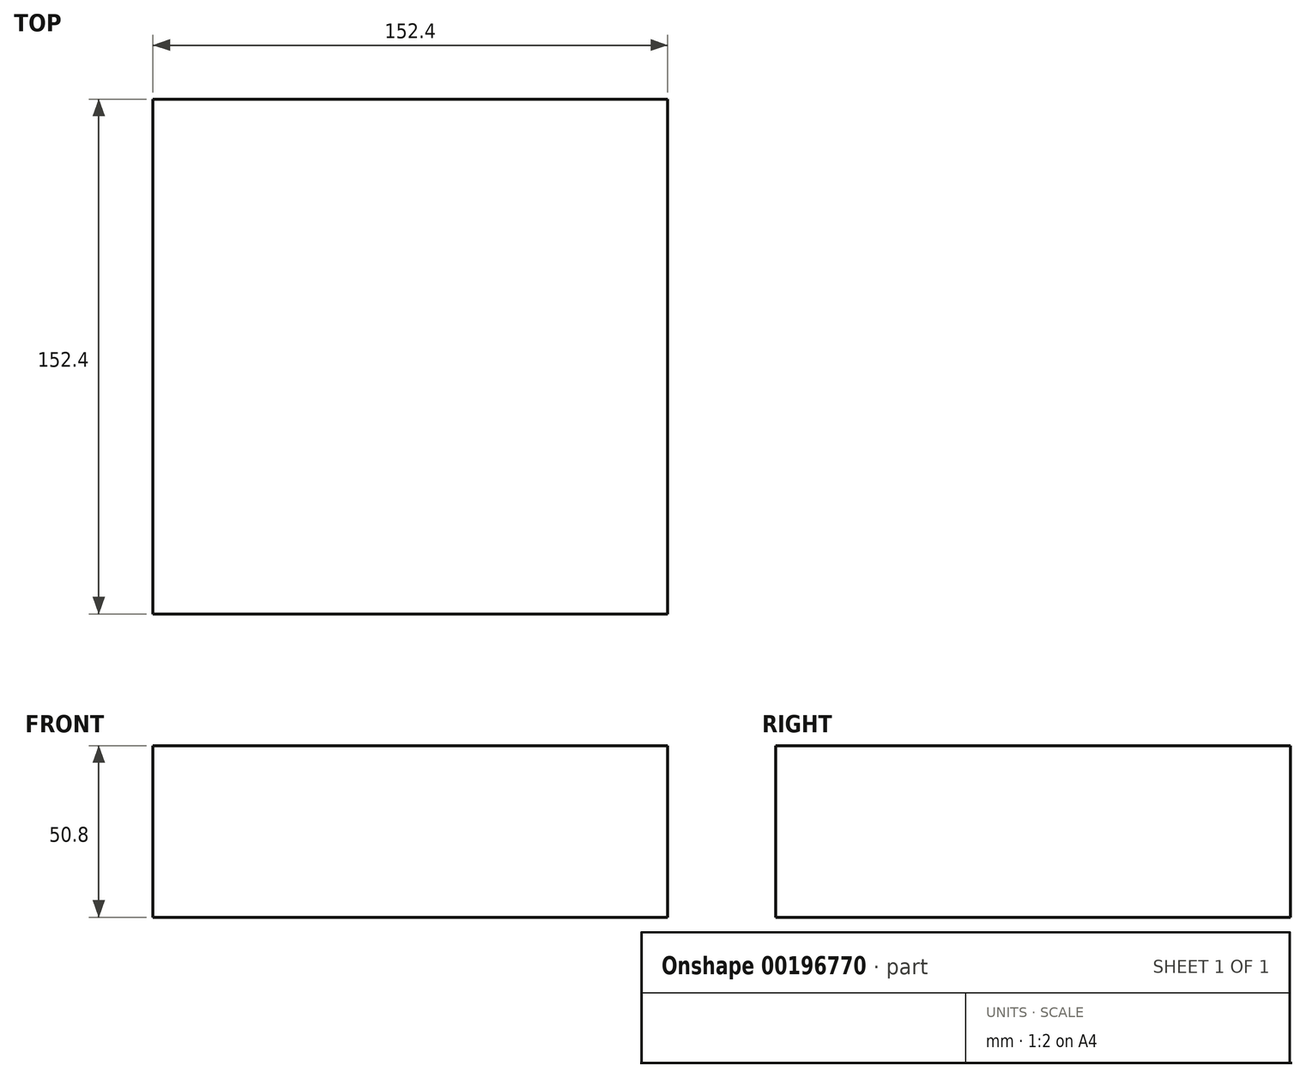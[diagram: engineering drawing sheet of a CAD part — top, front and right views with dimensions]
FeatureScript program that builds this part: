
annotation { "Feature Type Name" : "Feature", "Feature Type Description" : "" }
export const myFeature = defineFeature(function(context is Context, id is Id, definition is map)
    precondition{}
    {
        {
            var Q0;
            Q0=qCreatedBy(makeId("Top.planeOp"),FACE);
            var sketch = newSketch(context, id + "F0", { "sketchPlane" : qUnion([Q0])});
            skLineSegment(sketch, "E0.bottom", {"start": v(-76.59, 76.21) * mm, "end": v(75.81, 76.21) * mm});
            skLineSegment(sketch, "E0.top", {"start": v(-76.59, -76.19) * mm, "end": v(75.81, -76.19) * mm});
            skLineSegment(sketch, "E0.left", {"start": v(-76.59, 76.21) * mm, "end": v(-76.59, -76.19) * mm});
            skLineSegment(sketch, "E0.right", {"start": v(75.81, 76.21) * mm, "end": v(75.81, -76.19) * mm});
            skSolve(sketch);
        }
        {
            var Q0;
            Q0 = qSketchRegion(id + "F0", true);
            extrude(context, id + "F1", {"entities" : qUnion([Q0]), "depth" : 50.8 * mm});
        }
    });
